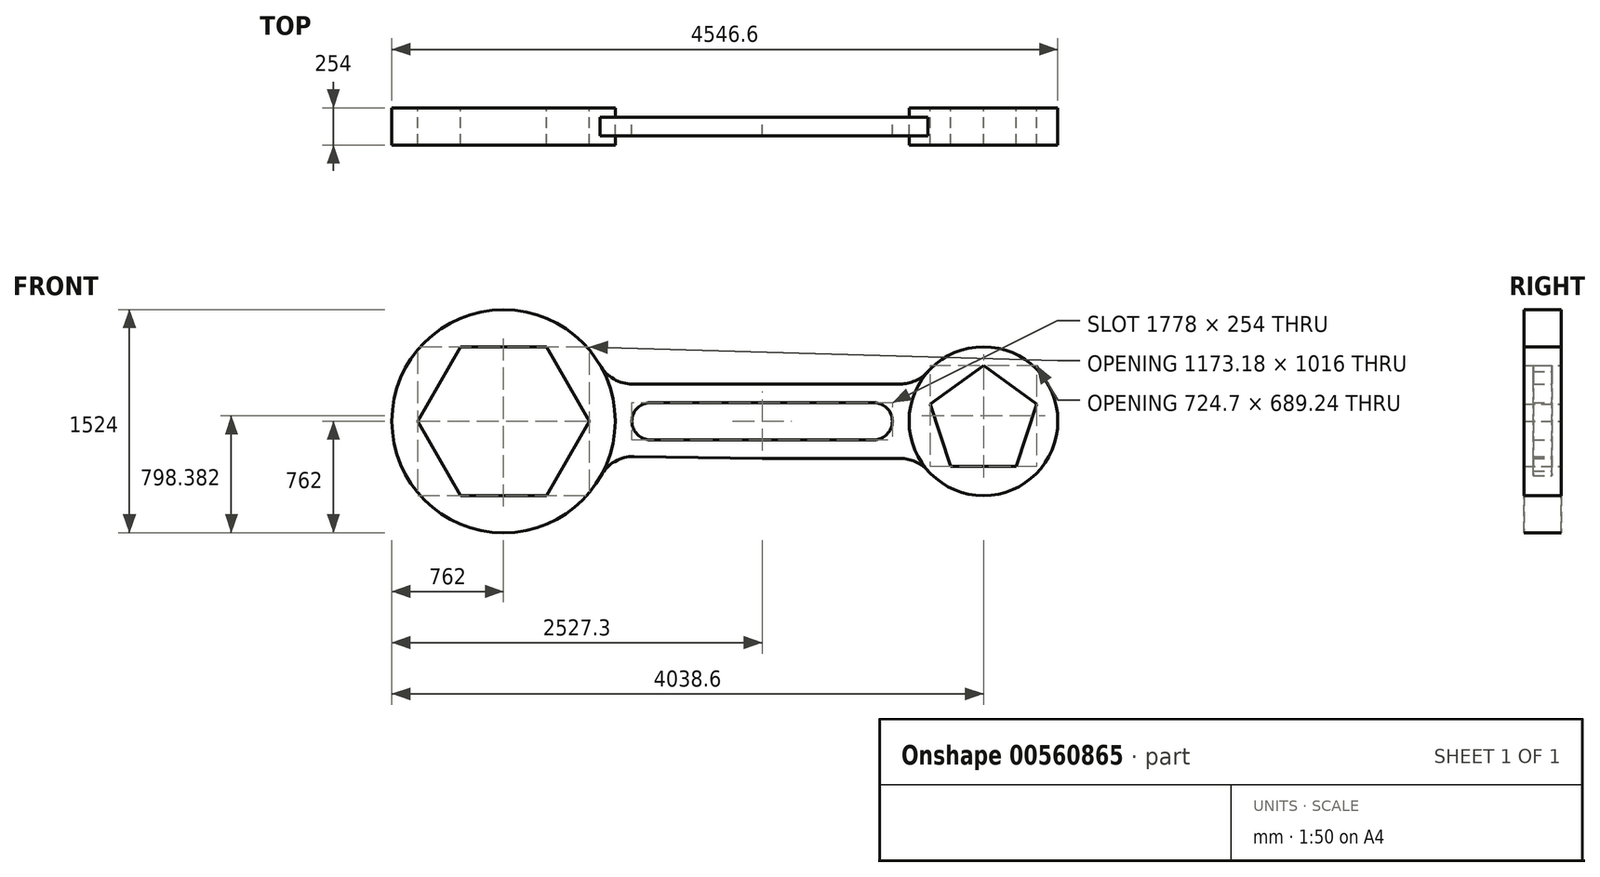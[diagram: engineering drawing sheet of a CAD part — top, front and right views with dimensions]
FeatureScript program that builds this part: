
annotation { "Feature Type Name" : "Feature", "Feature Type Description" : "" }
export const myFeature = defineFeature(function(context is Context, id is Id, definition is map)
    precondition{}
    {
        {
            var Q0;
            Q0=qCreatedBy(makeId("Front.planeOp"),FACE);
            var sketch = newSketch(context, id + "F0", { "sketchPlane" : qUnion([Q0])});
            skCircle(sketch, "E0", {"center": v(0, 0) * mm, "radius": 762 * mm});
            skCircle(sketch, "E1", {"center": v(3276.6, 0) * mm, "radius": 508 * mm});
            skPoint(sketch, "E2.orphan", {"position": v(751.34, 127) * mm});
            skLineSegment(sketch, "E3", {"start": v(1765.3, 127) * mm, "end": v(1003.3, 127) * mm});
            skLineSegment(sketch, "E4", {"start": v(1003.3, -127) * mm, "end": v(2527.3, -127) * mm});
            skLineSegment(sketch, "E5", {"start": v(2527.3, 127) * mm, "end": v(1765.3, 127) * mm});
            skArc(sketch, "E6", {"start": v(1003.3, 127) * mm, "mid": v(876.3, 0) * mm, "end": v(1003.3, -127) * mm});
            skArc(sketch, "E7", {"start": v(2527.3, -127) * mm, "mid": v(2654.3, 0) * mm, "end": v(2527.3, 127) * mm});
            skPoint(sketch, "E8.orphan", {"position": v(876.3, 127) * mm});
            skPoint(sketch, "E9.orphan", {"position": v(876.3, -127) * mm});
            skPoint(sketch, "E10.orphan", {"position": v(2654.3, 127) * mm});
            skPoint(sketch, "E11.orphan", {"position": v(2654.3, -127) * mm});
            skPoint(sketch, "E12.endSnap0", {"position": v(1765.3, -127) * mm});
            skLineSegment(sketch, "E13", {"start": v(1765.3, -254) * mm, "end": v(2708.64, -254) * mm});
            skLineSegment(sketch, "E14", {"start": v(1765.3, -254) * mm, "end": v(890.76, -241.34) * mm});
            skLineSegment(sketch, "E15", {"start": v(1765.3, 254) * mm, "end": v(2708.64, 254) * mm});
            skLineSegment(sketch, "E16", {"start": v(1765.3, 254) * mm, "end": v(879.88, 254) * mm});
            skArc(sketch, "E17", {"start": v(659.91, 381) * mm, "mid": v(752.88, 288.03) * mm, "end": v(879.88, 254) * mm});
            skArc(sketch, "E18", {"start": v(890.76, -241.34) * mm, "mid": v(760.1, -275.34) * mm, "end": v(665.31, -371.49) * mm});
            skArc(sketch, "E19", {"start": v(2708.64, 254) * mm, "mid": v(2812.33, 276.13) * mm, "end": v(2897.96, 338.67) * mm});
            skArc(sketch, "E20", {"start": v(2897.96, -338.67) * mm, "mid": v(2812.33, -276.13) * mm, "end": v(2708.64, -254) * mm});
            skCircle(sketch, "E21.cCircle", {"center": v(0, 0) * mm, "radius": 508 * mm, "construction": true});
            skLineSegment(sketch, "E21.0", {"start": v(-293.3, 508) * mm, "end": v(293.3, 508) * mm});
            skLineSegment(sketch, "E21.1", {"start": v(293.3, 508) * mm, "end": v(586.59, 0) * mm});
            skLineSegment(sketch, "E21.2", {"start": v(586.59, 0) * mm, "end": v(293.3, -508) * mm});
            skLineSegment(sketch, "E21.3", {"start": v(293.3, -508) * mm, "end": v(-293.3, -508) * mm});
            skLineSegment(sketch, "E21.4", {"start": v(-293.3, -508) * mm, "end": v(-586.59, 0) * mm});
            skLineSegment(sketch, "E21.5", {"start": v(-586.59, 0) * mm, "end": v(-293.3, 508) * mm});
            skPoint(sketch, "E21.0.midPoint", {"position": v(0, 508) * mm});
            skCircle(sketch, "E22.cCircle", {"center": v(3276.6, 0) * mm, "radius": 308.24 * mm, "construction": true});
            skLineSegment(sketch, "E22.0", {"start": v(3500.55, -308.24) * mm, "end": v(3052.65, -308.24) * mm});
            skLineSegment(sketch, "E22.1", {"start": v(3052.65, -308.24) * mm, "end": v(2914.25, 117.74) * mm});
            skLineSegment(sketch, "E22.2", {"start": v(2914.25, 117.74) * mm, "end": v(3276.6, 381) * mm});
            skLineSegment(sketch, "E22.3", {"start": v(3276.6, 381) * mm, "end": v(3638.95, 117.74) * mm});
            skLineSegment(sketch, "E22.4", {"start": v(3638.95, 117.74) * mm, "end": v(3500.55, -308.24) * mm});
            skPoint(sketch, "E22.0.midPoint", {"position": v(3276.6, -308.24) * mm});
            skSolve(sketch);
        }
        {
            var Q0;
            Q0=makeQuery(id+"F0.imprint","IMPRINT",FACE,{"disambiguationData":[TD([[makeQuery(id+"F0.imprint","IMPRINT",EDGE,{"derivedFrom":sQuery(id+"F0.wireOp",EDGE,"E21.0")}),1.0]])]});
            var Q1;
            Q1=makeQuery(id+"F0.imprint","IMPRINT",FACE,{"disambiguationData":[TD([[makeQuery(id+"F0.imprint","IMPRINT",EDGE,{"derivedFrom":sQuery(id+"F0.wireOp",EDGE,"E22.0")}),1.0]])]});
            extrude(context, id + "F1", {"entities" : qUnion([Q0, Q1]), "depth" : 254 * mm, "offsetDistance" : 25.4 * mm, "symmetric" : true});
        }
        {
            var Q0;
            Q0=makeQuery(id+"F0.imprint","IMPRINT",FACE,{"disambiguationData":[TD([[makeQuery(id+"F0.imprint","IMPRINT",EDGE,{"derivedFrom":sQuery(id+"F0.wireOp",EDGE,"E3")}),-1.0]])]});
            extrude(context, id + "F2", {"entities" : qUnion([Q0]), "depth" : 127 * mm, "offsetDistance" : 25.4 * mm, "symmetric" : true});
        }
    });
